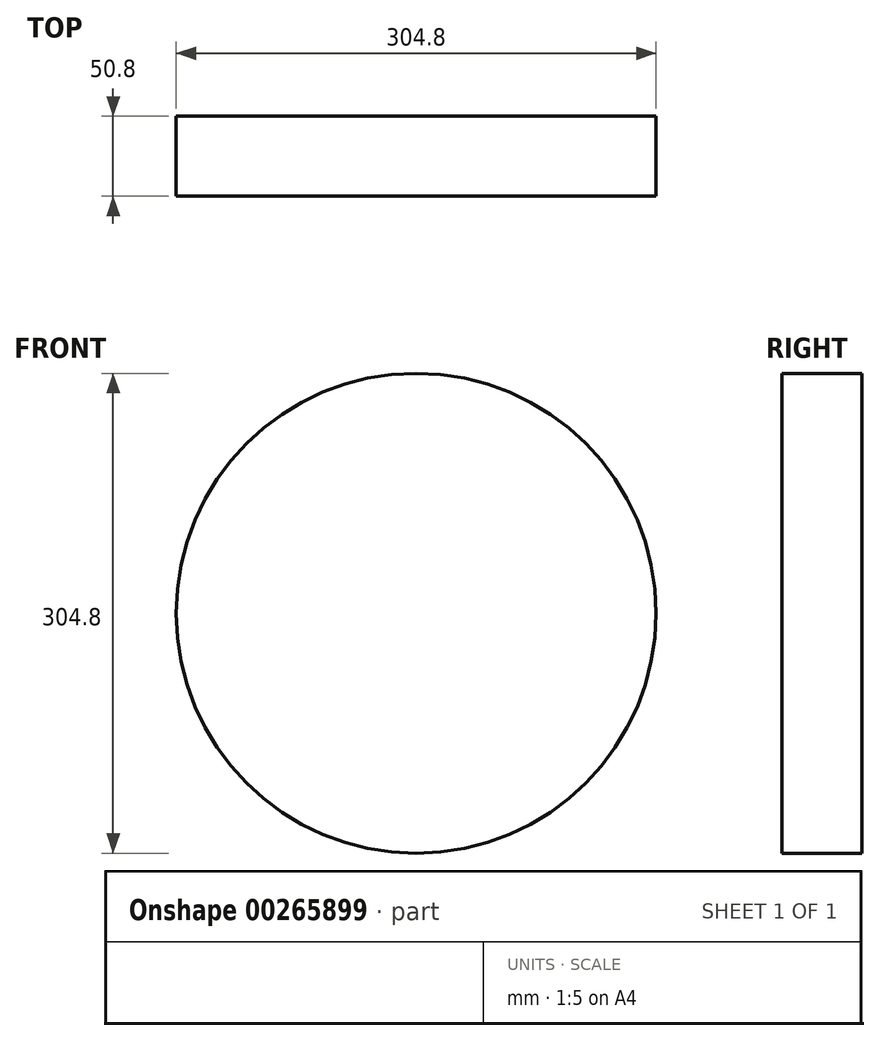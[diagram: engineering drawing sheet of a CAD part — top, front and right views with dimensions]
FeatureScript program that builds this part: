
annotation { "Feature Type Name" : "Feature", "Feature Type Description" : "" }
export const myFeature = defineFeature(function(context is Context, id is Id, definition is map)
    precondition{}
    {
        {
            var Q0;
            Q0=qCreatedBy(makeId("Front.planeOp"),FACE);
            var sketch = newSketch(context, id + "F0", { "sketchPlane" : qUnion([Q0])});
            skCircle(sketch, "E0", {"center": v(3.9, 0) * mm, "radius": 152.4 * mm});
            skSolve(sketch);
        }
        {
            var Q0;
            Q0=makeQuery(id+"F0.imprint","IMPRINT",FACE,{"disambiguationData":[TD([[makeQuery(id+"F0.imprint","IMPRINT",EDGE,{"derivedFrom":sQuery(id+"F0.wireOp",EDGE,"E0")}),1.0]])]});
            extrude(context, id + "F1", {"entities" : qUnion([Q0]), "depth" : 50.8 * mm});
        }
    });
